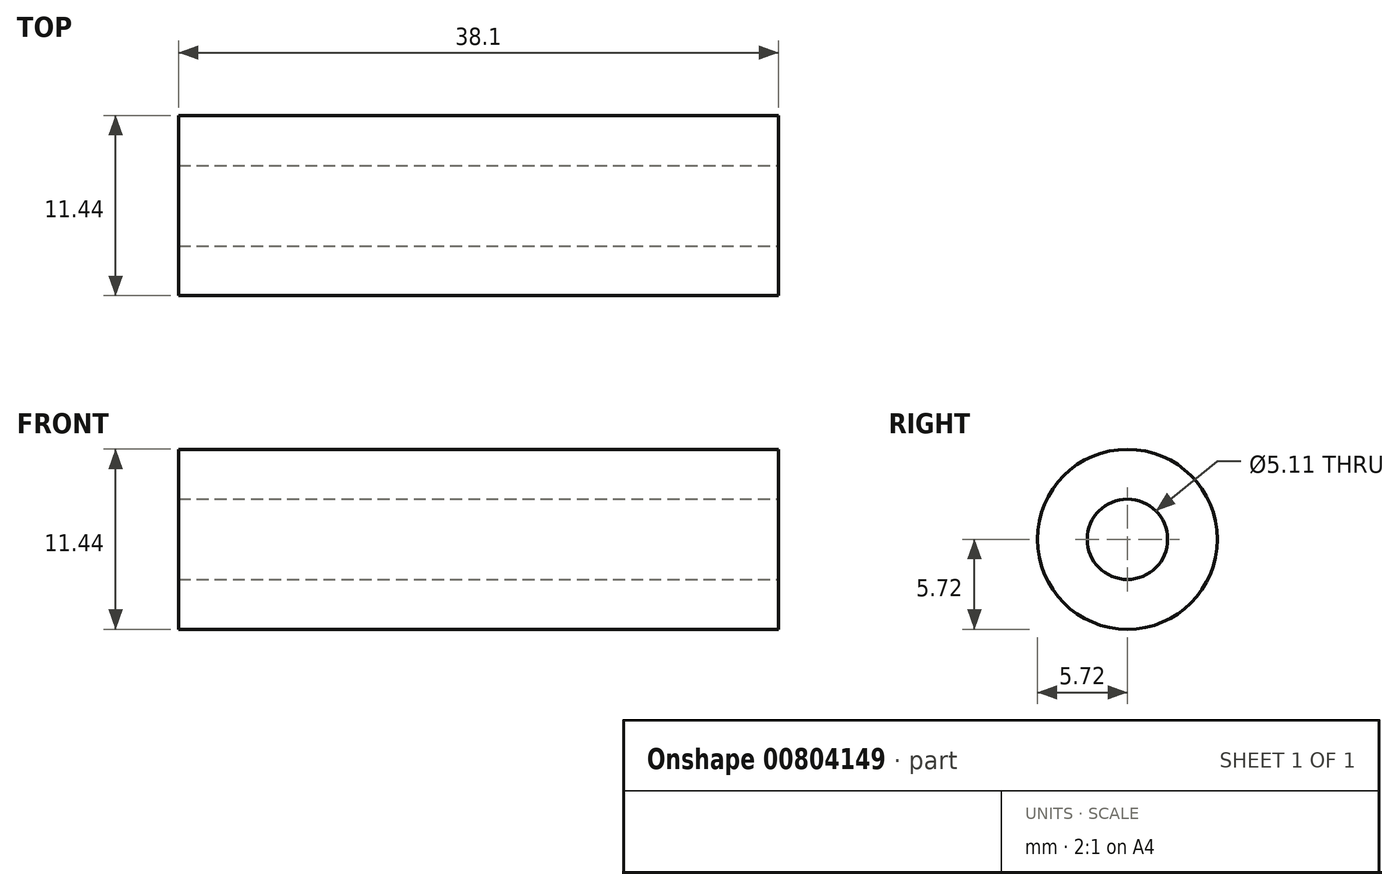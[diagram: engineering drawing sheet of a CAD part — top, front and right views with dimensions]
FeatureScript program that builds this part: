
annotation { "Feature Type Name" : "Feature", "Feature Type Description" : "" }
export const myFeature = defineFeature(function(context is Context, id is Id, definition is map)
    precondition{}
    {
        {
            var Q0;
            Q0=qCreatedBy(makeId("Right.planeOp"),FACE);
            var sketch = newSketch(context, id + "F0", { "sketchPlane" : qUnion([Q0])});
            skCircle(sketch, "E0", {"center": v(0, 0) * mm, "radius": 5.72 * mm});
            skSolve(sketch);
        }
        {
            var Q0;
            Q0 = qSketchRegion(id + "F0", true);
            extrude(context, id + "F1", {"entities" : qUnion([Q0]), "depth" : 38.1 * mm, "offsetDistance" : 25.4 * mm});
        }
        {
            var Q0;
            Q0=makeQuery(id+"F1.opExtrude","CAP_FACE",FACE,{"disambiguationData":[OSD([sQuery(id+"F0.wireOp",EDGE,"E0")])],"isStart":false});
            var sketch = newSketch(context, id + "F2", { "sketchPlane" : qUnion([Q0])});
            skPoint(sketch, "E1", {"position": v(0, 0) * mm});
            skSolve(sketch);
        }
        {
            var Q0;
            Q0=sQuery(id+"F2.wireOp",VERTEX,"E1");
            var Q1;
            Q1=makeQuery(id+"F1.opExtrude","SWEPT_BODY",BODY,{"disambiguationData":[OSD([sQuery(id+"F0.wireOp",EDGE,"E0")])]});
            hole(context, id + "F3", {"style" : HoleStyle.SIMPLE, "endStyle" : HoleEndStyle.THROUGH, "standardTappedOrClearance" : lookupTablePath({ "fit" : "Normal (ASME)", "standard" : "ANSI", "size" : "#10", "type" : "Clearance" }), "standardBlindInLast" : lookupTablePath({ "fit" : "Free", "standard" : "ANSI", "size" : "#10", "type" : "Clearance" }), "holeDiameter" : 5.1 * mm, "majorDiameter" : 6.35 * mm, "tappedDepth" : 9.52 * mm, "tapClearance" : 3, "startFromSketch" : true, "locations" : qUnion([Q0]), "scope" : qUnion([Q1])});
        }
    });
